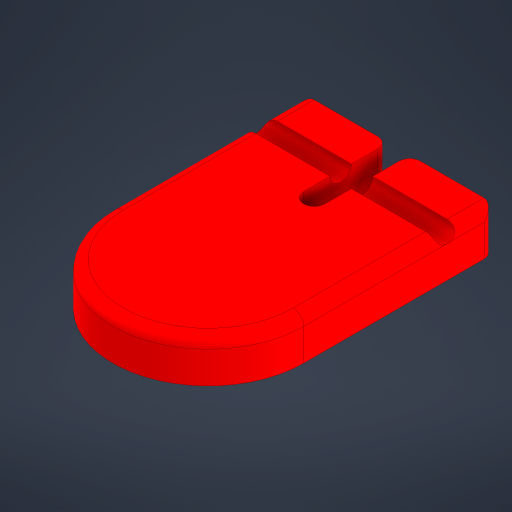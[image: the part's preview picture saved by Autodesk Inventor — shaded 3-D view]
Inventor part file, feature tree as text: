
AUTODESK INVENTOR PART (.ipt)
format: ipt  version: 2023.4 (Build 274418000, 418)  size: 228,352 bytes
history: native  units: mm
features: extrude x2, sketch x1, fillet x1
ambient origin geometry x8: Origin, YZ Plane, XZ Plane, XY Plane, X Axis, Y Axis, Z Axis, Center Point
bodies: Solid1 (feature_tree)
feature tree (4):
  sketch  "Sketch1"  dims[d0=45.0mm d1=45.0mm d2=5.0mm d3=5.0mm d4=7.5mm d5=0.0mm d6=2.5mm d7=0.0mm d8=2.5mm]
  extrude  "Extrusion1"  Depth=2.5mm
  extrude  "Extrusion2"  Depth=5.0mm
  fillet  "Fillet1"  Radius=5.0mm
